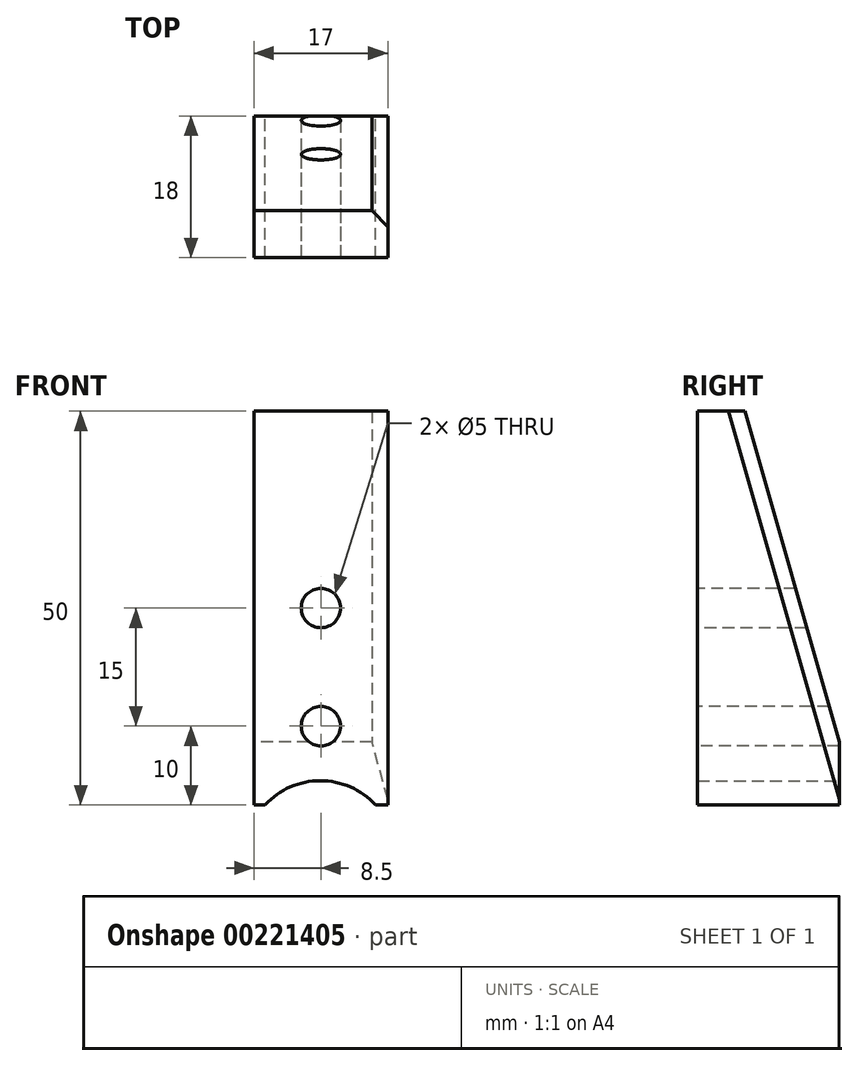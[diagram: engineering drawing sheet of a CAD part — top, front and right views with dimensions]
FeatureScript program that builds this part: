
annotation { "Feature Type Name" : "Feature", "Feature Type Description" : "" }
export const myFeature = defineFeature(function(context is Context, id is Id, definition is map)
    precondition{}
    {
        {
            var Q0;
            Q0=qCreatedBy(makeId("Front.planeOp"),FACE);
            var sketch = newSketch(context, id + "F0", { "sketchPlane" : qUnion([Q0])});
            skLineSegment(sketch, "E0.bottom", {"start": v(0, 0) * mm, "end": v(-17, 0) * mm});
            skLineSegment(sketch, "E0.top", {"start": v(0, 50) * mm, "end": v(-17, 50) * mm});
            skLineSegment(sketch, "E0.left", {"start": v(0, 0) * mm, "end": v(0, 50) * mm});
            skLineSegment(sketch, "E0.right", {"start": v(-17, 0) * mm, "end": v(-17, 50) * mm});
            skSolve(sketch);
        }
        {
            var Q0;
            Q0 = qSketchRegion(id + "F0", true);
            var Q1;
            Q1=makeQuery(id+"F0.imprint","IMPRINT",FACE,{"disambiguationData":[TD([[makeQuery(id+"F0.imprint","IMPRINT",EDGE,{"derivedFrom":sQuery(id+"F0.wireOp",EDGE,"E0.bottom")}),-1.0]])]});
            extrude(context, id + "F1", {"entities" : qUnion([Q0, Q1]), "depth" : 18 * mm});
        }
        {
            var Q0;
            Q0=makeQuery(id+"F1.opExtrude","CAP_FACE",FACE,{"disambiguationData":[OSD([sQuery(id+"F0.wireOp",EDGE,"E0.bottom"),sQuery(id+"F0.wireOp",EDGE,"E0.top"),sQuery(id+"F0.wireOp",EDGE,"E0.left"),sQuery(id+"F0.wireOp",EDGE,"E0.right")])],"isStart":false});
            var sketch = newSketch(context, id + "F2", { "sketchPlane" : qUnion([Q0])});
            skPoint(sketch, "E1", {"position": v(-8.5, 10) * mm});
            skPoint(sketch, "E1.positionSnap0", {"position": v(-8.5, 0) * mm});
            skPoint(sketch, "E2", {"position": v(-8.5, 25) * mm});
            skSolve(sketch);
        }
        {
            var Q0;
            Q0=sQuery(id+"F2.wireOp",VERTEX,"E1");
            var Q1;
            Q1=sQuery(id+"F2.wireOp",VERTEX,"E2");
            var Q2;
            Q2=makeQuery(id+"F1.opExtrude","SWEPT_BODY",BODY,{"disambiguationData":[OSD([sQuery(id+"F0.wireOp",EDGE,"E0.bottom"),sQuery(id+"F0.wireOp",EDGE,"E0.top"),sQuery(id+"F0.wireOp",EDGE,"E0.left"),sQuery(id+"F0.wireOp",EDGE,"E0.right")])]});
            hole(context, id + "F3", {"style" : HoleStyle.SIMPLE, "endStyle" : HoleEndStyle.BLIND, "holeDiameter" : 5 * mm, "holeDepth" : 25 * mm, "startFromSketch" : true, "locations" : qUnion([Q0, Q1]), "scope" : qUnion([Q2])});
        }
        {
            var Q0;
            Q0=makeQuery(id+"F1.opExtrude","SWEPT_FACE",FACE,{"disambiguationData":[OSD([sQuery(id+"F0.wireOp",EDGE,"E0.right")])]});
            var sketch = newSketch(context, id + "F4", { "sketchPlane" : qUnion([Q0])});
            skLineSegment(sketch, "E3", {"start": v(0, 8) * mm, "end": v(12, 50) * mm});
            skSolve(sketch);
        }
        {
            var Q0;
            {var subQ0=sQuery(id+"F4.wireOp",EDGE,"E3");Q0=makeQuery(id+"F4.imprint","IMPRINT",FACE,{"disambiguationData":[TD([[makeQuery(id+"F4.imprint","IMPRINT",EDGE,{"derivedFrom":subQ0}),1.0]])]});}
            extrude(context, id + "F5", {"entities" : qUnion([Q0]), "operationType" : NewBodyOperationType.REMOVE, "oppositeDirection" : true, "depth" : 25 * mm});
        }
        {
            var Q0;
            Q0=qCreatedBy(makeId("Front.planeOp"),FACE);
            var sketch = newSketch(context, id + "F6", { "sketchPlane" : qUnion([Q0])});
            skPoint(sketch, "E4", {"position": v(-8.58, -6.72) * mm});
            skCircle(sketch, "E5", {"center": v(-8.58, -6.72) * mm, "radius": 9.5 * mm});
            skSolve(sketch);
        }
        {
            var Q0;
            Q0=makeQuery(id+"F6.imprint","IMPRINT",FACE,{"disambiguationData":[TD([[makeQuery(id+"F6.imprint","IMPRINT",EDGE,{"derivedFrom":sQuery(id+"F6.wireOp",EDGE,"E5")}),1.0]])]});
            extrude(context, id + "F7", {"entities" : qUnion([Q0]), "operationType" : NewBodyOperationType.REMOVE, "oppositeDirection" : true, "depth" : 25 * mm});
        }
        {
            var Q0;
            Q0=qCreatedBy(makeId("Front.planeOp"),FACE);
            var sketch = newSketch(context, id + "F8", { "sketchPlane" : qUnion([Q0])});
            skPoint(sketch, "E6", {"position": v(-8.27, -6.72) * mm});
            skCircle(sketch, "E7", {"center": v(-8.27, -6.72) * mm, "radius": 9.5 * mm});
            skCircle(sketch, "E8", {"center": v(11, -6.72) * mm, "radius": 1.63 * mm});
            skSolve(sketch);
        }
        {
            var Q0;
            Q0 = qSketchRegion(id + "F8", true);
            var Q1;
            Q1=makeQuery(id+"F8.imprint","IMPRINT",FACE,{"disambiguationData":[TD([[makeQuery(id+"F8.imprint","IMPRINT",EDGE,{"derivedFrom":sQuery(id+"F8.wireOp",EDGE,"E7")}),1.0]])]});
            extrude(context, id + "F9", {"entities" : qUnion([Q0, Q1]), "operationType" : NewBodyOperationType.REMOVE, "oppositeDirection" : true, "depth" : 25 * mm});
        }
        {
            var Q0;
            Q0=makeQuery(id+"F1.opExtrude","CAP_FACE",FACE,{"disambiguationData":[OSD([sQuery(id+"F0.wireOp",EDGE,"E0.bottom"),sQuery(id+"F0.wireOp",EDGE,"E0.top"),sQuery(id+"F0.wireOp",EDGE,"E0.left"),sQuery(id+"F0.wireOp",EDGE,"E0.right")])],"isStart":true});
            var sketch = newSketch(context, id + "F10", { "sketchPlane" : qUnion([Q0])});
            skPoint(sketch, "E9", {"position": v(8.58, -6.43) * mm});
            skCircle(sketch, "E10", {"center": v(8.58, -6.43) * mm, "radius": 9.5 * mm});
            skSolve(sketch);
        }
        {
            var Q0;
            Q0 = qSketchRegion(id + "F10", true);
            var Q1;
            {var subQ0=sQuery(id+"F10.wireOp",EDGE,"E10");var subQ1=makeQuery(id+"F1.opExtrude","CAP_EDGE",EDGE,{"disambiguationData":[OSD([sQuery(id+"F0.wireOp",EDGE,"E0.bottom")])],"isStart":true});var subQ2=makeQuery(id+"F10.imprint","INTERSECT",VERTEX,{"disambiguationData":[OD(0.0)],"derivedFrom":[subQ1,subQ0]});Q1=makeQuery(id+"F10.imprint","IMPRINT",FACE,{"disambiguationData":[TD([[makeQuery(id+"F10.imprint","IMPRINT",EDGE,{"disambiguationData":[TD([[subQ2,-1.0]])],"derivedFrom":subQ0}),1.0]])]});}
            extrude(context, id + "F11", {"entities" : qUnion([Q0, Q1]), "operationType" : NewBodyOperationType.REMOVE, "oppositeDirection" : true, "depth" : 25 * mm});
        }
        {
            var Q0;
            Q0=makeQuery(id+"F5.boolean.opBoolean","INTERSECT",EDGE,{"derivedFrom":[makeQuery(id+"F1.opExtrude","SWEPT_FACE",FACE,{"disambiguationData":[OSD([sQuery(id+"F0.wireOp",EDGE,"E0.left")])]}),makeQuery(id+"F5.opExtrude","SWEPT_FACE",FACE,{"disambiguationData":[OSD([sQuery(id+"F4.wireOp",EDGE,"E3")])]})]});
            var Q1;
            Q1=makeQuery(id+"F5.boolean.opBoolean","COPY",EDGE,{"derivedFrom":makeQuery(id+"F5.opExtrude","CAP_EDGE",EDGE,{"disambiguationData":[OSD([sQuery(id+"F4.wireOp",EDGE,"E3")])],"isStart":true})});
            chamfer(context, id + "F12", {"entities" : qUnion([Q0, Q1]), "width" : 2 * mm, "tangentPropagation" : true});
        }
    });
